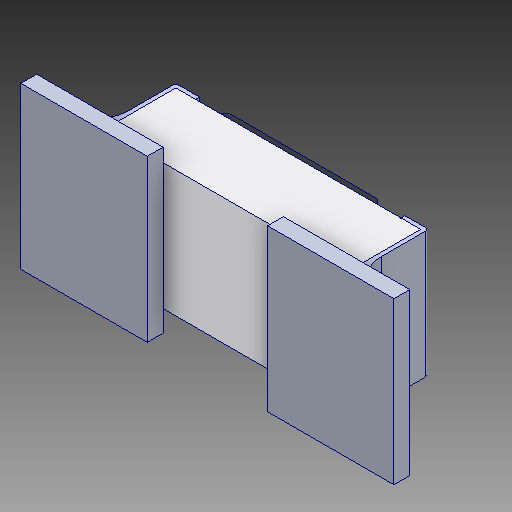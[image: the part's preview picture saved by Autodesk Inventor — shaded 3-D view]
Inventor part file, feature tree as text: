
AUTODESK INVENTOR PART (.ipt)
format: ipt  version: 2018 (Build 220112000, 112)  size: 215,552 bytes
history: native  units: mm
features: other x2, fillet x2
ambient origin geometry x8: Origin, YZ Plane, XZ Plane, XY Plane, X Axis, Y Axis, Z Axis, Center Point
bodies: Volumenkörper1 (feature_tree), Volumenkörper2 (feature_tree), Volumenkörper3 (feature_tree), Volumenkörper4 (feature_tree)
feature tree (4):
  other  "Boss-Extrude1"
  other  "Boss-Extrude4"
  fillet  "Fillet6"  [1 undecoded]
  fillet  "Fillet5"  [1 undecoded]
note: 2 required parameter values undecoded (feature->parameter linkage not recoverable at this tier; creation-order binding heuristic only, values carry confidence <= 0.55)
